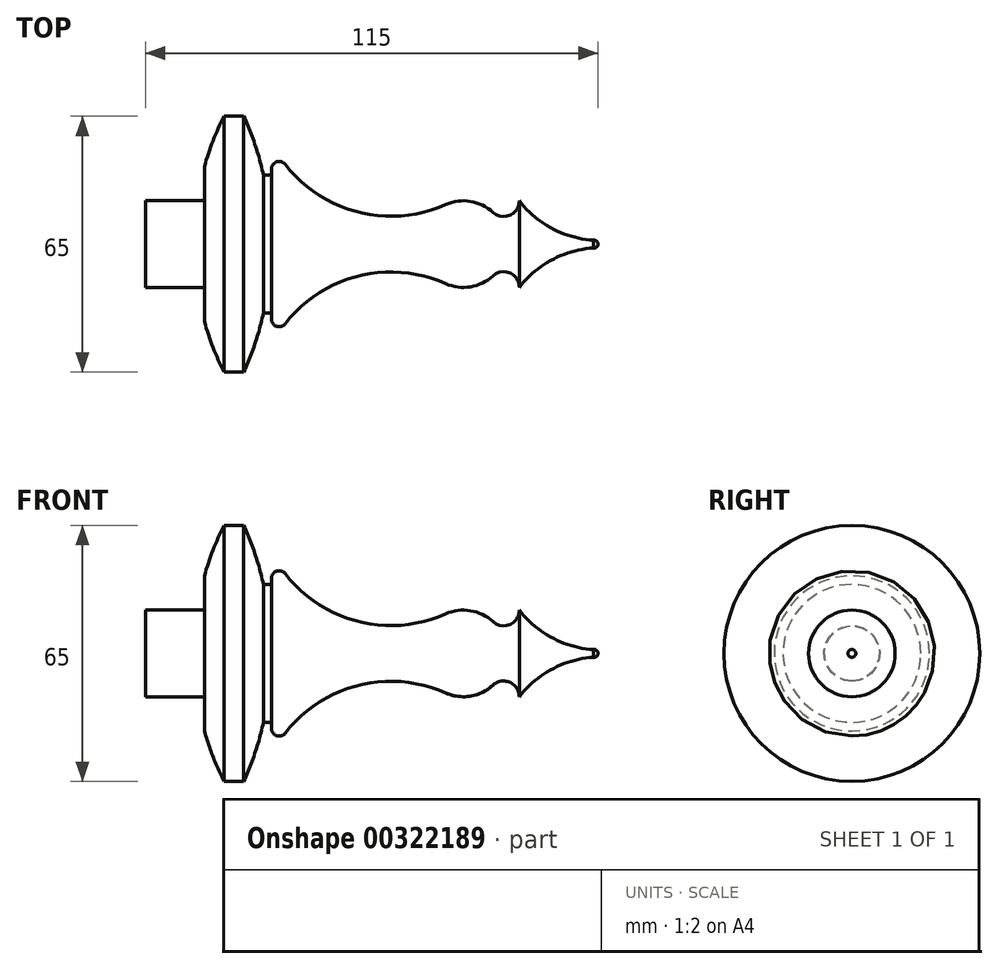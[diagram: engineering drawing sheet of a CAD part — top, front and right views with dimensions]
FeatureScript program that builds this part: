
annotation { "Feature Type Name" : "Feature", "Feature Type Description" : "" }
export const myFeature = defineFeature(function(context is Context, id is Id, definition is map)
    precondition{}
    {
        {
            var Q0;
            Q0=qCreatedBy(makeId("Front.planeOp"),FACE);
            var sketch = newSketch(context, id + "F0", { "sketchPlane" : qUnion([Q0])});
            skLineSegment(sketch, "E0.top", {"start": v(0, 11) * mm, "end": v(15, 11) * mm});
            skLineSegment(sketch, "E0.left", {"start": v(0, 0) * mm, "end": v(0, 11) * mm});
            skLineSegment(sketch, "E0.right", {"start": v(15, 11) * mm, "end": v(15, 19.72) * mm});
            skLineSegment(sketch, "E1", {"start": v(25, 0) * mm, "end": v(25, 32.5) * mm});
            skLineSegment(sketch, "E2", {"start": v(30, 0) * mm, "end": v(30, 17.5) * mm});
            skLineSegment(sketch, "E3", {"start": v(20, 0) * mm, "end": v(20, 32.5) * mm});
            skArc(sketch, "E4", {"start": v(20, 32.5) * mm, "mid": v(17.2, 26.23) * mm, "end": v(15, 19.72) * mm});
            skLineSegment(sketch, "E5", {"start": v(25, 32.5) * mm, "end": v(20, 32.5) * mm});
            skLineSegment(sketch, "E6", {"start": v(32, 17.5) * mm, "end": v(32, 0) * mm});
            skArc(sketch, "E7", {"start": v(35.58, 20.23) * mm, "mid": v(33.35, 20.9) * mm, "end": v(32, 19) * mm});
            skLineSegment(sketch, "E8", {"start": v(32, 17.5) * mm, "end": v(32, 19) * mm});
            skPoint(sketch, "E9.center.orphan", {"position": v(70.46, 0) * mm});
            skArc(sketch, "E10", {"start": v(115, 0) * mm, "mid": v(114.64, 0.77) * mm, "end": v(113.82, 0.98) * mm});
            skLineSegment(sketch, "E11", {"start": v(95, 0) * mm, "end": v(95, 11) * mm});
            skArc(sketch, "E12", {"start": v(95, 11) * mm, "mid": v(103.33, 3.97) * mm, "end": v(113.82, 0.98) * mm});
            skPoint(sketch, "E13.MirrorCS.end.orphan", {"position": v(95, -11) * mm});
            skPoint(sketch, "E14.start.orphan", {"position": v(93.33, 7) * mm});
            skArc(sketch, "E15", {"start": v(91, 7) * mm, "mid": v(93.83, 8.17) * mm, "end": v(95, 11) * mm});
            skPoint(sketch, "E16.orphan", {"position": v(82.51, 11) * mm});
            skArc(sketch, "E17", {"start": v(88.28, 8.07) * mm, "mid": v(92.6, 7.33) * mm, "end": v(95, 11) * mm});
            skArc(sketch, "E18", {"start": v(88.28, 8.07) * mm, "mid": v(82.6, 10.85) * mm, "end": v(76.31, 10.04) * mm});
            skArc(sketch, "E19", {"start": v(30, 17.5) * mm, "mid": v(27.91, 25.14) * mm, "end": v(25, 32.5) * mm});
            skPoint(sketch, "E19.third.point", {"position": v(-112.35, 0) * mm});
            skArc(sketch, "E20", {"start": v(35.58, 20.23) * mm, "mid": v(54.19, 8.1) * mm, "end": v(76.31, 10.04) * mm});
            skPoint(sketch, "E20.first.point", {"position": v(76.31, 10.04) * mm});
            skPoint(sketch, "E21.end.orphan", {"position": v(115, 4.05) * mm});
            skLineSegment(sketch, "E22", {"start": v(115, 0) * mm, "end": v(0, 0) * mm});
            skLineSegment(sketch, "E23", {"start": v(32, 17.5) * mm, "end": v(30, 17.5) * mm});
            skSolve(sketch);
        }
        {
            var Q0;
            Q0=makeQuery(id+"F0.imprint","IMPRINT",FACE,{"disambiguationData":[TD([[makeQuery(id+"F0.imprint","IMPRINT",EDGE,{"derivedFrom":sQuery(id+"F0.wireOp",EDGE,"E0.top")}),-1.0]])]});
            var Q1;
            {var subQ0=sQuery(id+"F0.wireOp",EDGE,"E1");Q1=makeQuery(id+"F0.imprint","IMPRINT",FACE,{"disambiguationData":[TD([[makeQuery(id+"F0.imprint","IMPRINT",EDGE,{"derivedFrom":subQ0}),1.0]])]});}
            var Q2;
            {var subQ0=sQuery(id+"F0.wireOp",EDGE,"E1");Q2=makeQuery(id+"F0.imprint","IMPRINT",FACE,{"disambiguationData":[TD([[makeQuery(id+"F0.imprint","IMPRINT",EDGE,{"derivedFrom":subQ0}),-1.0]])]});}
            var Q3;
            {var subQ0=sQuery(id+"F0.wireOp",EDGE,"E2");Q3=makeQuery(id+"F0.imprint","IMPRINT",FACE,{"disambiguationData":[TD([[makeQuery(id+"F0.imprint","IMPRINT",EDGE,{"derivedFrom":subQ0}),-1.0]])]});}
            var Q4;
            {var subQ1=sQuery(id+"F0.wireOp",EDGE,"E6");Q4=makeQuery(id+"F0.imprint","IMPRINT",FACE,{"disambiguationData":[TD([[makeQuery(id+"F0.imprint","IMPRINT",EDGE,{"derivedFrom":subQ1}),1.0]])]});}
            var Q5;
            {var subQ0=sQuery(id+"F0.wireOp",EDGE,"E10");Q5=makeQuery(id+"F0.imprint","IMPRINT",FACE,{"disambiguationData":[TD([[makeQuery(id+"F0.imprint","IMPRINT",EDGE,{"derivedFrom":subQ0}),1.0]])]});}
            var Q6;
            Q6=sQuery(id+"F0.wireOp",EDGE,"E22");
            revolve(context, id + "F1", {"entities" : qUnion([Q0, Q1, Q2, Q3, Q4, Q5]), "axis" : qUnion([Q6]), "revolveType" : RevolveType.FULL});
        }
    });
